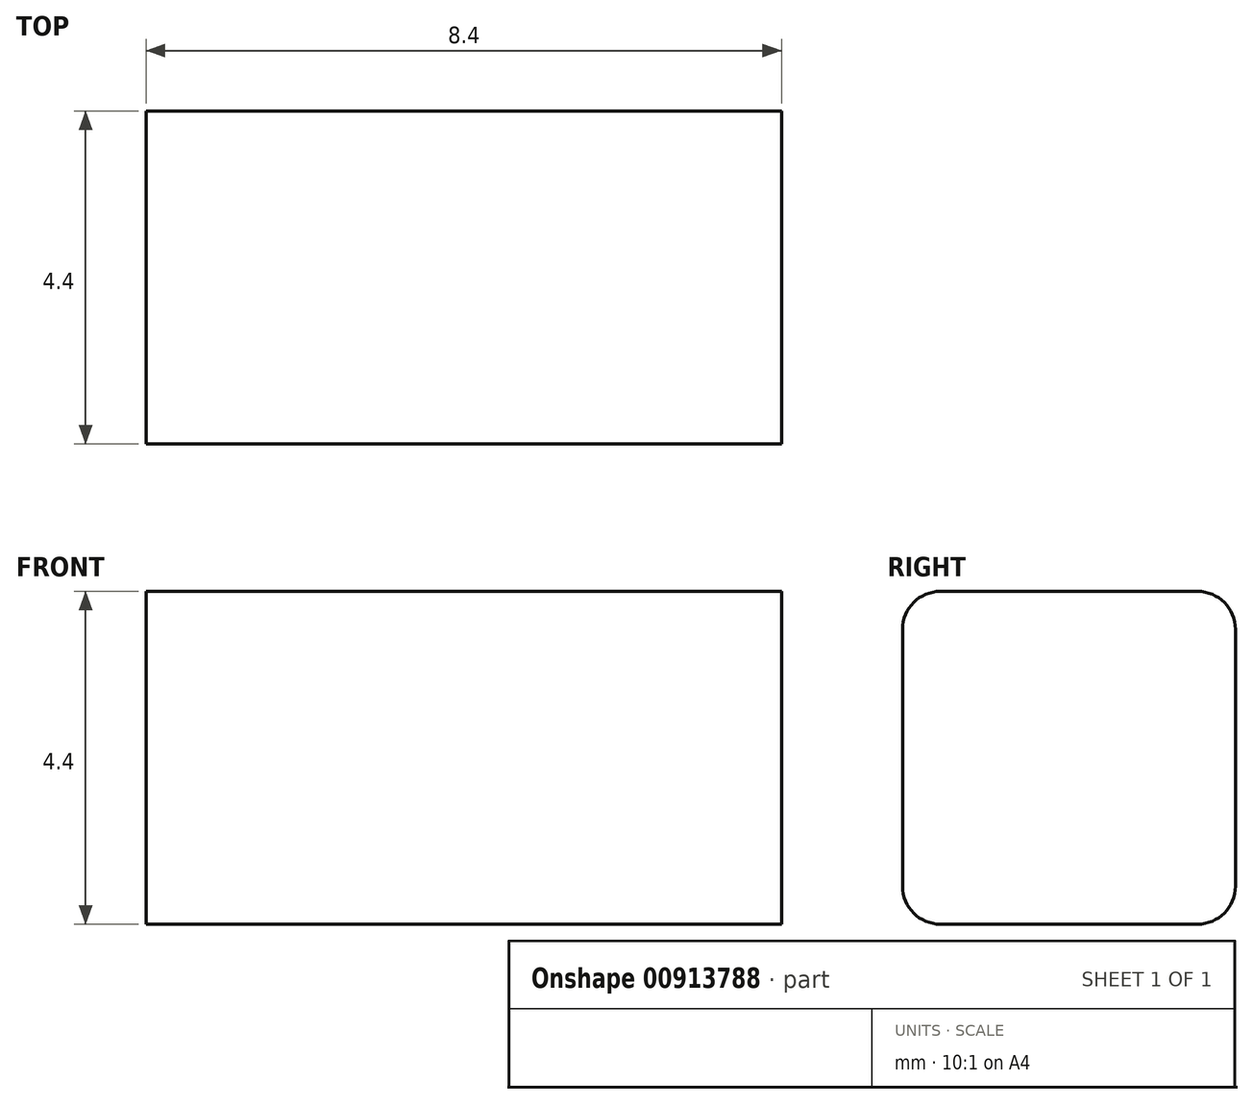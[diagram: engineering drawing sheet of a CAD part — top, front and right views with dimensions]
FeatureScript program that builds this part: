
annotation { "Feature Type Name" : "Feature", "Feature Type Description" : "" }
export const myFeature = defineFeature(function(context is Context, id is Id, definition is map)
    precondition{}
    {
        {
            var Q0;
            Q0=qCreatedBy(makeId("Right.planeOp"),FACE);
            var sketch = newSketch(context, id + "F0", { "sketchPlane" : qUnion([Q0])});
            skPoint(sketch, "E0.middle", {"position": v(0, 0) * mm});
            skLineSegment(sketch, "E1.bottom", {"start": v(-1.7, 2.2) * mm, "end": v(1.7, 2.2) * mm});
            skLineSegment(sketch, "E1.top", {"start": v(-1.7, -2.2) * mm, "end": v(1.7, -2.2) * mm});
            skLineSegment(sketch, "E1.left", {"start": v(-2.2, 1.7) * mm, "end": v(-2.2, -1.7) * mm});
            skLineSegment(sketch, "E1.right", {"start": v(2.2, 1.7) * mm, "end": v(2.2, -1.7) * mm});
            skPoint(sketch, "E2.visualSharp", {"position": v(-2.2, 2.2) * mm});
            skArc(sketch, "E2.filletArc", {"start": v(-1.7, 2.2) * mm, "mid": v(-2.05, 2.05) * mm, "end": v(-2.2, 1.7) * mm});
            skPoint(sketch, "E3.visualSharp", {"position": v(-2.2, -2.2) * mm});
            skArc(sketch, "E3.filletArc", {"start": v(-2.2, -1.7) * mm, "mid": v(-2.05, -2.05) * mm, "end": v(-1.7, -2.2) * mm});
            skPoint(sketch, "E4.visualSharp", {"position": v(2.2, -2.2) * mm});
            skArc(sketch, "E4.filletArc", {"start": v(1.7, -2.2) * mm, "mid": v(2.05, -2.05) * mm, "end": v(2.2, -1.7) * mm});
            skPoint(sketch, "E5.visualSharp", {"position": v(2.2, 2.2) * mm});
            skArc(sketch, "E5.filletArc", {"start": v(2.2, 1.7) * mm, "mid": v(2.05, 2.05) * mm, "end": v(1.7, 2.2) * mm});
            skSolve(sketch);
        }
        {
            var Q0;
            Q0 = qSketchRegion(id + "F0", true);
            extrude(context, id + "F1", {"entities" : qUnion([Q0]), "depth" : 8.4 * mm, "offsetDistance" : 25.4 * mm});
        }
    });
